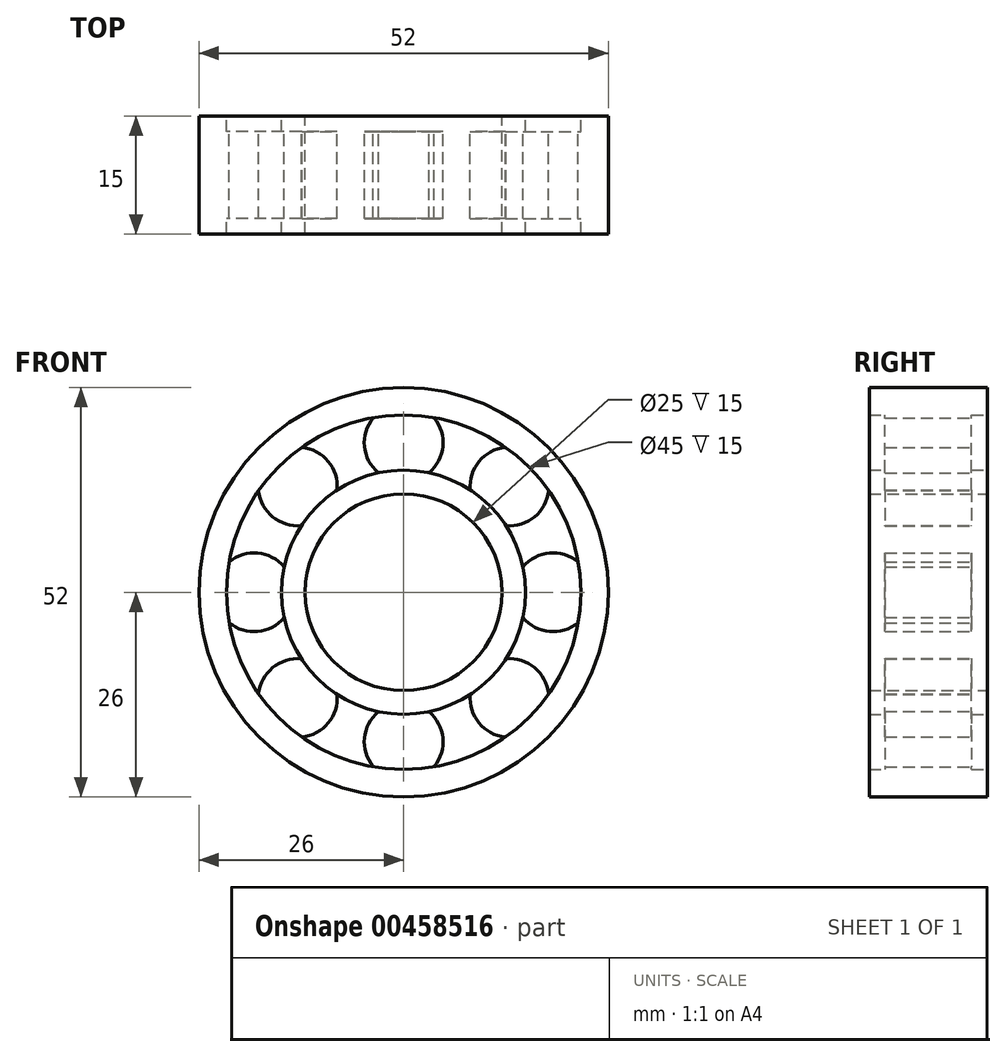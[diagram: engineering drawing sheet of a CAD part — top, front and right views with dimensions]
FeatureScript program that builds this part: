
annotation { "Feature Type Name" : "Feature", "Feature Type Description" : "" }
export const myFeature = defineFeature(function(context is Context, id is Id, definition is map)
    precondition{}
    {
        {
            var Q0;
            Q0=qCreatedBy(makeId("Front.planeOp"),FACE);
            var sketch = newSketch(context, id + "F0", { "sketchPlane" : qUnion([Q0])});
            skCircle(sketch, "E0", {"center": v(0, 0) * mm, "radius": 12.5 * mm});
            skCircle(sketch, "E1", {"center": v(0, 0) * mm, "radius": 15.5 * mm});
            skSolve(sketch);
        }
        {
            var Q0;
            Q0=makeQuery(id+"F0.imprint","IMPRINT",FACE,{"disambiguationData":[TD([[makeQuery(id+"F0.imprint","IMPRINT",EDGE,{"derivedFrom":sQuery(id+"F0.wireOp",EDGE,"E0")}),-1.0]])]});
            extrude(context, id + "F1", {"entities" : qUnion([Q0]), "depth" : 15 * mm, "symmetric" : true});
        }
        {
            var Q0;
            Q0=qCreatedBy(makeId("Front.planeOp"),FACE);
            var sketch = newSketch(context, id + "F2", { "sketchPlane" : qUnion([Q0])});
            skCircle(sketch, "E2", {"center": v(0, 0) * mm, "radius": 26 * mm});
            skCircle(sketch, "E3", {"center": v(0, 0) * mm, "radius": 22.5 * mm});
            skSolve(sketch);
        }
        {
            var Q0;
            Q0=makeQuery(id+"F2.imprint","IMPRINT",FACE,{"disambiguationData":[TD([[makeQuery(id+"F2.imprint","IMPRINT",EDGE,{"derivedFrom":sQuery(id+"F2.wireOp",EDGE,"E2")}),1.0]])]});
            extrude(context, id + "F3", {"entities" : qUnion([Q0]), "depth" : 15 * mm, "symmetric" : true});
        }
        {
            var Q0;
            Q0=qCreatedBy(makeId("Front.planeOp"),FACE);
            var sketch = newSketch(context, id + "F4", { "sketchPlane" : qUnion([Q0])});
            skCircle(sketch, "E4", {"center": v(0, 19) * mm, "radius": 5 * mm});
            skCircle(sketch, "E5", {"center": v(19, 0) * mm, "radius": 5 * mm});
            skCircle(sketch, "E6", {"center": v(0, -19) * mm, "radius": 5 * mm});
            skCircle(sketch, "E7", {"center": v(-19, 0) * mm, "radius": 5 * mm});
            skCircle(sketch, "E8", {"center": v(-13.44, -13.44) * mm, "radius": 5 * mm});
            skCircle(sketch, "E9", {"center": v(-13.44, 13.44) * mm, "radius": 5 * mm});
            skCircle(sketch, "E10", {"center": v(13.44, 13.44) * mm, "radius": 5 * mm});
            skCircle(sketch, "E11", {"center": v(13.44, -13.44) * mm, "radius": 5 * mm});
            skSolve(sketch);
        }
        {
            var Q0;
            Q0=makeQuery(id+"F4.imprint","IMPRINT",FACE,{"disambiguationData":[TD([[makeQuery(id+"F4.imprint","IMPRINT",EDGE,{"derivedFrom":sQuery(id+"F4.wireOp",EDGE,"E9")}),1.0]])]});
            var Q1;
            Q1=makeQuery(id+"F4.imprint","IMPRINT",FACE,{"disambiguationData":[TD([[makeQuery(id+"F4.imprint","IMPRINT",EDGE,{"derivedFrom":sQuery(id+"F4.wireOp",EDGE,"E4")}),1.0]])]});
            var Q2;
            Q2=makeQuery(id+"F4.imprint","IMPRINT",FACE,{"disambiguationData":[TD([[makeQuery(id+"F4.imprint","IMPRINT",EDGE,{"derivedFrom":sQuery(id+"F4.wireOp",EDGE,"E10")}),1.0]])]});
            var Q3;
            Q3=makeQuery(id+"F4.imprint","IMPRINT",FACE,{"disambiguationData":[TD([[makeQuery(id+"F4.imprint","IMPRINT",EDGE,{"derivedFrom":sQuery(id+"F4.wireOp",EDGE,"E5")}),1.0]])]});
            var Q4;
            Q4=makeQuery(id+"F4.imprint","IMPRINT",FACE,{"disambiguationData":[TD([[makeQuery(id+"F4.imprint","IMPRINT",EDGE,{"derivedFrom":sQuery(id+"F4.wireOp",EDGE,"E7")}),1.0]])]});
            var Q5;
            Q5=makeQuery(id+"F4.imprint","IMPRINT",FACE,{"disambiguationData":[TD([[makeQuery(id+"F4.imprint","IMPRINT",EDGE,{"derivedFrom":sQuery(id+"F4.wireOp",EDGE,"E8")}),1.0]])]});
            var Q6;
            Q6=makeQuery(id+"F4.imprint","IMPRINT",FACE,{"disambiguationData":[TD([[makeQuery(id+"F4.imprint","IMPRINT",EDGE,{"derivedFrom":sQuery(id+"F4.wireOp",EDGE,"E11")}),1.0]])]});
            var Q7;
            Q7=makeQuery(id+"F4.imprint","IMPRINT",FACE,{"disambiguationData":[TD([[makeQuery(id+"F4.imprint","IMPRINT",EDGE,{"derivedFrom":sQuery(id+"F4.wireOp",EDGE,"E6")}),1.0]])]});
            var Q8;
            Q8=sQuery(id+"F4.wireOp",EDGE,"E4");
            var Q9;
            Q9=sQuery(id+"F4.wireOp",EDGE,"E9");
            var Q10;
            Q10=sQuery(id+"F4.wireOp",EDGE,"E7");
            var Q11;
            Q11=sQuery(id+"F4.wireOp",EDGE,"E8");
            var Q12;
            Q12=sQuery(id+"F4.wireOp",EDGE,"E10");
            var Q13;
            Q13=sQuery(id+"F4.wireOp",EDGE,"E5");
            var Q14;
            Q14=sQuery(id+"F4.wireOp",EDGE,"E11");
            var Q15;
            Q15=sQuery(id+"F4.wireOp",EDGE,"E6");
            extrude(context, id + "F5", {"entities" : qUnion([Q0, Q1, Q2, Q3, Q4, Q5, Q6, Q7]), "operationType" : NewBodyOperationType.ADD, "surfaceEntities" : qUnion([Q8, Q9, Q10, Q11, Q12, Q13, Q14, Q15]), "depth" : 11 * mm, "offsetDistance" : 25 * mm, "symmetric" : true});
        }
    });
